# Revit family: Platek_Pico
name_source: partatom
category: Apparecchi per illuminazione
revit_build: Autodesk Revit 2017 (Build: 20160225_1515(x64)
units: mm (PartAtom-declared; Revit-internal decimal feet)

## family parameters
Condiviso = No
Host = Superficie
Punto di calcolo locali = No
Quota connettore circolare = Usa diametro
Sorgente d'illuminazione = Sì
Taglio con vuoti quando caricato = No
Tipo di parte = Normale

## types (2) — shared parameters
Angolo inclinazione = -90.00°
Body = PLK_Inox
CRI = >80
Cable Lenght = 0.5m (2X0,5mm^2)
Colour Temperature = 3000 K
Commenti sul tipo = Pedestrian areas, Facades, Columns, Trees
Current = 0 A
Descrizione = Outdoor Lighting, Ground/Floor Recessed
Diffuse Type = 2mm flat tempered extra clear gass 500Kg
Dimmable = NO
Emetti da diametro cerchio = 13 mm  [stored 0.0426509 ft]
Energy Efficiency Rating = A/A+/A++
Filtro dei colori = 16777215
IK Rating = IK07
IP Rating = IP68 Full dry (2m)
Immagine tipo = pico.jpg
Insulation Class = 3
LED Protection = Surge Protection Included
Lampada = LED
Light Source = PLK_Light Source
Luminaire Wattage = 1 W
Manufacturer Comment = Full Inox/Drive Over/Walk Over
Modello = Pico Full Inox
Mounting Type = In-ground recessed/Ceiling Concrete Recessed/Wall Recessed
Nota chiave = Recessed box excluded and IP68 connector to be ordered separately, Other Led colors available on request
PLATEK FInishes = Full Inox
Plastic = PLK_Plastic_Black
Power Supply Unit = Power Supply Remote, Power Supply excluded to be ordered separately
Product Dimension = Ø 21mm/H44mm
Product Documentation Link = http://www.platek.eu
Product Page URL = http://www.platek.eu
Produttore = PLATEK SRL
Prospetto di default = 1219 mm
Rendi la forma visibile nel rendering = No
URL = www.platek.eu
Variazione temperatura colore lampada con luminosità attenuata = <Nessuno>
Voltage Output = 12 V

## per-type parameters (varying)
| type | Beam Angle | Codice assieme | File diagramma fotometrico | Luminaire Luminous Flux | Luminaire Luminous Intensity | PLATEK Article Code |
| 8495011_1,4W_LED_3000K_Full Inox | 20.00° | 8495011 (Full Inox)+8945040+8956109 or 8956091 or 8956103 | 8495011.IES | 85 lm | 670 cd | 8495011 |
| 8495015_1,4W_LED_3000K_Full Inox | 80.00° | 8495015 (Full Inox)+8945040+8956109 or 8956091 or 8956103 | 8495015.IES | 45 lm | 25 cd | 8495015 |

note: [stored X ft] marks values corroborated as IEEE doubles in the binary element streams (Revit-internal decimal feet)
